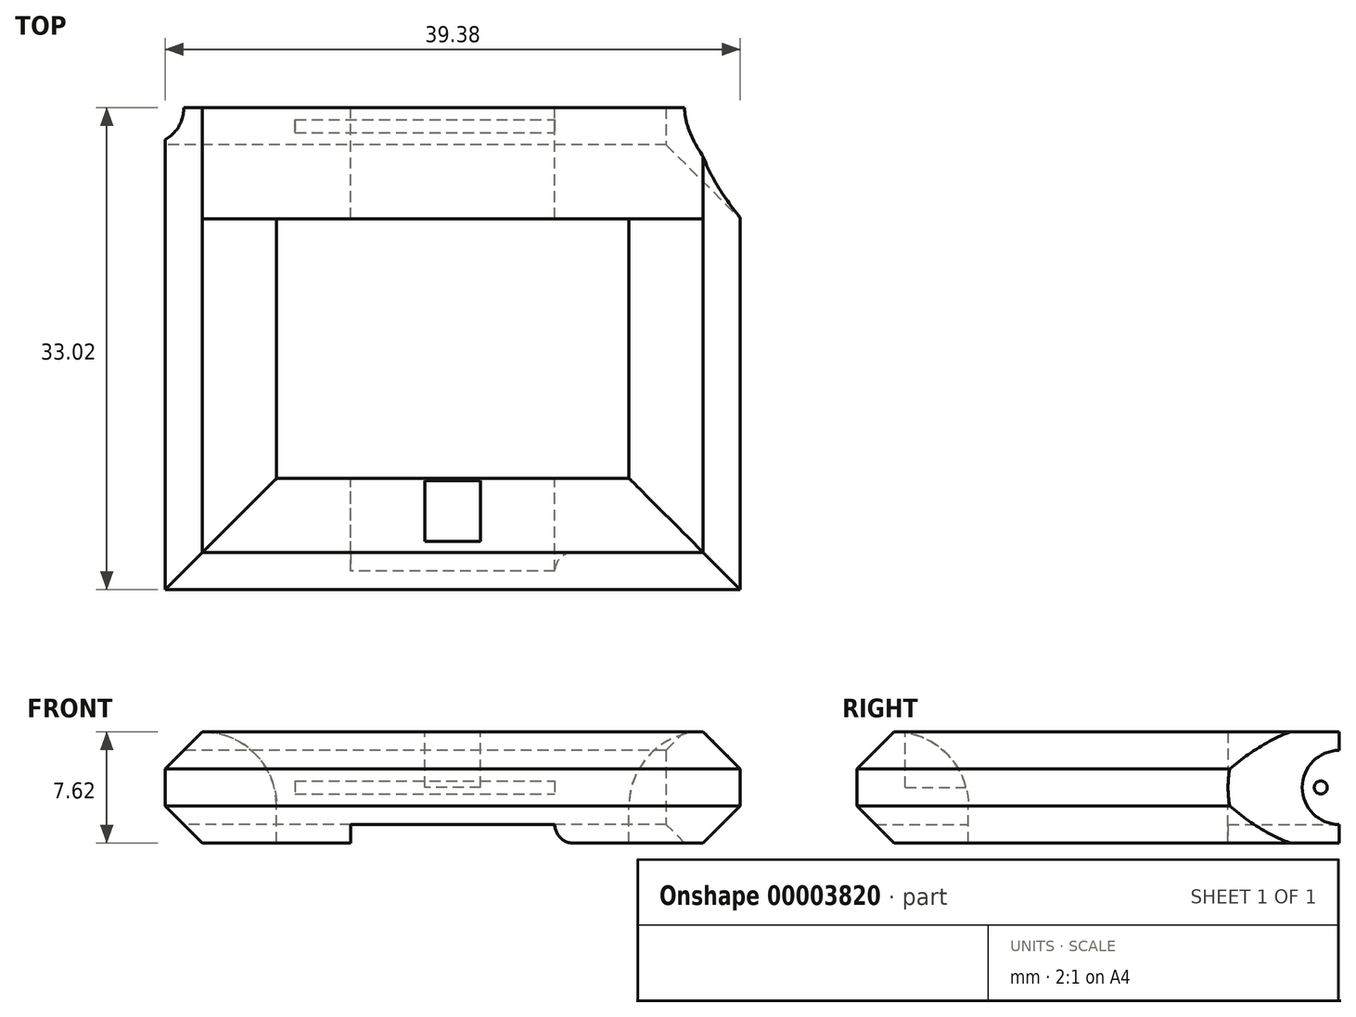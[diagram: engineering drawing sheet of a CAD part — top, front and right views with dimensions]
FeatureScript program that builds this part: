
annotation { "Feature Type Name" : "Feature", "Feature Type Description" : "" }
export const myFeature = defineFeature(function(context is Context, id is Id, definition is map)
    precondition{}
    {
        {
            var Q0;
            Q0=qCreatedBy(makeId("Right.planeOp"),FACE);
            var sketch = newSketch(context, id + "F0", { "sketchPlane" : qUnion([Q0])});
            skLineSegment(sketch, "E0.rect.bottom", {"start": v(3.8, -3.8) * mm, "end": v(-3.81, -3.81) * mm});
            skLineSegment(sketch, "E0.rect.top", {"start": v(3.8, 3.81) * mm, "end": v(-3.81, 3.81) * mm});
            skLineSegment(sketch, "E0.rect.left", {"start": v(3.8, -3.8) * mm, "end": v(3.81, 3.81) * mm});
            skLineSegment(sketch, "E0.rect.right", {"start": v(-3.81, -3.81) * mm, "end": v(-3.81, 3.8) * mm});
            skPoint(sketch, "E0.rect.middle", {"position": v(0, 0) * mm});
            skSolve(sketch);
        }
        {
            var Q0;
            Q0=qCreatedBy(makeId("Top.planeOp"),FACE);
            var sketch = newSketch(context, id + "F1", { "sketchPlane" : qUnion([Q0])});
            skLineSegment(sketch, "E1.bottom", {"start": v(15.87, 0) * mm, "end": v(-15.87, 0) * mm});
            skLineSegment(sketch, "E1.top", {"start": v(15.88, -25.4) * mm, "end": v(-15.87, -25.4) * mm});
            skLineSegment(sketch, "E1.left", {"start": v(15.88, 0) * mm, "end": v(15.88, -25.4) * mm});
            skLineSegment(sketch, "E1.right", {"start": v(-15.88, 0) * mm, "end": v(-15.87, -25.4) * mm});
            skSolve(sketch);
        }
        {
            var Q0;
            Q0=makeQuery(id+"F0.imprint","IMPRINT",FACE,{"disambiguationData":[TD([[makeQuery(id+"F0.imprint","IMPRINT",EDGE,{"derivedFrom":sQuery(id+"F0.wireOp",EDGE,"E0.rect.bottom")}),-1.0]])]});
            var Q1;
            Q1=sQuery(id+"F1.wireOp",EDGE,"E1.right");
            var Q2;
            Q2=sQuery(id+"F1.wireOp",EDGE,"E1.bottom");
            var Q3;
            Q3=sQuery(id+"F1.wireOp",EDGE,"E1.top");
            var Q4;
            Q4=sQuery(id+"F1.wireOp",EDGE,"E1.left");
            sweep(context, id + "F2", {"profiles" : qUnion([Q0]), "path" : qUnion([Q1, Q2, Q3, Q4])});
        }
        {
            var Q0;
            Q0=makeQuery(id+"F2.opSweep","SWEPT_FACE",FACE,{"disambiguationData":[OSD([sQuery(id+"F0.wireOp",EDGE,"E0.rect.left"),sQuery(id+"F1.wireOp",EDGE,"E1.right")])]});
            var sketch = newSketch(context, id + "F3", { "sketchPlane" : qUnion([Q0])});
            skArc(sketch, "E2", {"start": v(-3.81, -2.54) * mm, "mid": v(-1.27, 0) * mm, "end": v(-3.81, 2.54) * mm});
            skLineSegment(sketch, "E3", {"start": v(-3.81, 2.54) * mm, "end": v(-3.81, -2.54) * mm});
            skSolve(sketch);
        }
        {
            var Q0;
            Q0=makeQuery(id+"F3.imprint","IMPRINT",FACE,{"disambiguationData":[TD([[makeQuery(id+"F3.imprint","IMPRINT",EDGE,{"derivedFrom":sQuery(id+"F3.wireOp",EDGE,"E2")}),1.0]])]});
            var Q1;
            Q1=makeQuery(id+"F3.imprint","IMPRINT",FACE,{"disambiguationData":[TD([[makeQuery(id+"F3.imprint","IMPRINT",EDGE,{"derivedFrom":sQuery(id+"F3.wireOp",EDGE,"E2")}),1.0]])]});
            extrude(context, id + "F4", {"entities" : qUnion([Q0, Q1]), "operationType" : NewBodyOperationType.REMOVE, "endBound" : BoundingType.THROUGH_ALL, "oppositeDirection" : true, "depth" : 25.4 * mm});
        }
        {
            var Q0;
            Q0=makeQuery(id+"F2.opSweep","SWEPT_EDGE",EDGE,{"disambiguationData":[OSD([sQuery(id+"F0.wireOp",EDGE,"E0.rect.top"),sQuery(id+"F0.wireOp",EDGE,"E0.rect.left"),sQuery(id+"F1.wireOp",EDGE,"E1.left")])]});
            var Q1;
            Q1=makeQuery(id+"F2.opSweep","SWEPT_EDGE",EDGE,{"disambiguationData":[OSD([sQuery(id+"F0.wireOp",EDGE,"E0.rect.top"),sQuery(id+"F0.wireOp",EDGE,"E0.rect.left"),sQuery(id+"F1.wireOp",EDGE,"E1.top")])]});
            var Q2;
            Q2=makeQuery(id+"F2.opSweep","SWEPT_EDGE",EDGE,{"disambiguationData":[OSD([sQuery(id+"F0.wireOp",EDGE,"E0.rect.top"),sQuery(id+"F0.wireOp",EDGE,"E0.rect.left"),sQuery(id+"F1.wireOp",EDGE,"E1.right")])]});
            var Q3;
            Q3=makeQuery(id+"F2.opSweep","SWEPT_EDGE",EDGE,{"disambiguationData":[OSD([sQuery(id+"F0.wireOp",EDGE,"E0.rect.bottom"),sQuery(id+"F0.wireOp",EDGE,"E0.rect.left"),sQuery(id+"F1.wireOp",EDGE,"E1.right")])]});
            var Q4;
            Q4=makeQuery(id+"F2.opSweep","SWEPT_EDGE",EDGE,{"disambiguationData":[OSD([sQuery(id+"F0.wireOp",EDGE,"E0.rect.bottom"),sQuery(id+"F0.wireOp",EDGE,"E0.rect.left"),sQuery(id+"F1.wireOp",EDGE,"E1.top")])]});
            var Q5;
            Q5=makeQuery(id+"F2.opSweep","SWEPT_EDGE",EDGE,{"disambiguationData":[OSD([sQuery(id+"F0.wireOp",EDGE,"E0.rect.bottom"),sQuery(id+"F0.wireOp",EDGE,"E0.rect.left"),sQuery(id+"F1.wireOp",EDGE,"E1.left")])]});
            chamfer(context, id + "F5", {"entities" : qUnion([Q0, Q1, Q2, Q3, Q4, Q5]), "width" : 2.54 * mm, "tangentPropagation" : true});
        }
        {
            var Q0;
            Q0=makeQuery(id+"F2.opSweep","SWEPT_EDGE",EDGE,{"disambiguationData":[OSD([sQuery(id+"F0.wireOp",EDGE,"E0.rect.top"),sQuery(id+"F0.wireOp",EDGE,"E0.rect.right"),sQuery(id+"F1.wireOp",EDGE,"E1.top")])]});
            var Q1;
            Q1=makeQuery(id+"F2.opSweep","SWEPT_EDGE",EDGE,{"disambiguationData":[OSD([sQuery(id+"F0.wireOp",EDGE,"E0.rect.top"),sQuery(id+"F0.wireOp",EDGE,"E0.rect.right"),sQuery(id+"F1.wireOp",EDGE,"E1.right")])]});
            var Q2;
            Q2=makeQuery(id+"F2.opSweep","SWEPT_EDGE",EDGE,{"disambiguationData":[OSD([sQuery(id+"F0.wireOp",EDGE,"E0.rect.top"),sQuery(id+"F0.wireOp",EDGE,"E0.rect.right"),sQuery(id+"F1.wireOp",EDGE,"E1.left")])]});
            fillet(context, id + "F6", {"entities" : qUnion([Q0, Q1, Q2]), "radius" : 5.08 * mm, "tangentPropagation" : true, "allowEdgeOverflow" : false});
        }
        {
            var Q0;
            Q0=makeQuery(id+"F2.opSweep","SWEPT_FACE",FACE,{"disambiguationData":[OSD([sQuery(id+"F0.wireOp",EDGE,"E0.rect.top"),sQuery(id+"F1.wireOp",EDGE,"E1.bottom")])]});
            var sketch = newSketch(context, id + "F7", { "sketchPlane" : qUnion([Q0])});
            skLineSegment(sketch, "E4.bottom", {"start": v(-6.98, -3.81) * mm, "end": v(6.98, -3.81) * mm});
            skLineSegment(sketch, "E4.top", {"start": v(-6.98, -1.27) * mm, "end": v(6.98, -1.27) * mm});
            skLineSegment(sketch, "E4.left", {"start": v(-6.98, -3.81) * mm, "end": v(-6.98, -1.27) * mm});
            skLineSegment(sketch, "E4.right", {"start": v(6.98, -3.81) * mm, "end": v(6.98, -1.27) * mm});
            skSolve(sketch);
        }
        {
            var Q0;
            Q0=makeQuery(id+"F7.imprint","IMPRINT",FACE,{"disambiguationData":[TD([[makeQuery(id+"F7.imprint","IMPRINT",EDGE,{"derivedFrom":sQuery(id+"F7.wireOp",EDGE,"E4.bottom")}),-1.0]])]});
            extrude(context, id + "F8", {"entities" : qUnion([Q0]), "operationType" : NewBodyOperationType.REMOVE, "endBound" : BoundingType.THROUGH_ALL, "oppositeDirection" : true, "depth" : 25.4 * mm});
        }
        {
            var Q0;
            Q0=makeQuery(id+"F8.boolean.opBoolean","COPY",FACE,{"derivedFrom":makeQuery(id+"F8.opExtrude","SWEPT_FACE",FACE,{"disambiguationData":[OSD([sQuery(id+"F7.wireOp",EDGE,"E4.left")])]})});
            var sketch = newSketch(context, id + "F9", { "sketchPlane" : qUnion([Q0])});
            skCircle(sketch, "E5", {"center": v(-2.54, 0) * mm, "radius": 0.44 * mm});
            skSolve(sketch);
        }
        {
            var Q0;
            Q0=makeQuery(id+"F9.imprint","IMPRINT",FACE,{"disambiguationData":[TD([[makeQuery(id+"F9.imprint","IMPRINT",EDGE,{"derivedFrom":sQuery(id+"F9.wireOp",EDGE,"E5")}),1.0]])]});
            extrude(context, id + "F10", {"entities" : qUnion([Q0]), "operationType" : NewBodyOperationType.ADD, "depth" : 17.78 * mm});
        }
        {
            var Q0;
            Q0=makeQuery(id+"F8.boolean.opBoolean","COPY",EDGE,{"derivedFrom":makeQuery(id+"F8.opExtrude","CAP_EDGE",EDGE,{"disambiguationData":[OSD([sQuery(id+"F7.wireOp",EDGE,"E4.top")])],"isStart":true})});
            var Q1;
            Q1=makeQuery(id+"F8.boolean.opBoolean","COPY",EDGE,{"derivedFrom":makeQuery(id+"F8.opExtrude","SWEPT_EDGE",EDGE,{"disambiguationData":[OSD([sQuery(id+"F0.wireOp",EDGE,"E0.rect.top"),sQuery(id+"F0.wireOp",EDGE,"E0.rect.right"),sQuery(id+"F1.wireOp",EDGE,"E1.bottom"),sQuery(id+"F7.wireOp",EDGE,"E4.bottom"),sQuery(id+"F7.wireOp",EDGE,"E4.left")])]})});
            var Q2;
            Q2=makeQuery(id+"F8.boolean.opBoolean","COPY",EDGE,{"derivedFrom":makeQuery(id+"F8.opExtrude","SWEPT_EDGE",EDGE,{"disambiguationData":[OSD([sQuery(id+"F0.wireOp",EDGE,"E0.rect.top"),sQuery(id+"F0.wireOp",EDGE,"E0.rect.right"),sQuery(id+"F1.wireOp",EDGE,"E1.bottom"),sQuery(id+"F7.wireOp",EDGE,"E4.bottom"),sQuery(id+"F7.wireOp",EDGE,"E4.right")])]})});
            var Q3;
            Q3=makeQuery(id+"F8.boolean.opBoolean","INTERSECT",EDGE,{"derivedFrom":[makeQuery(id+"F2.opSweep","SWEPT_FACE",FACE,{"disambiguationData":[OSD([sQuery(id+"F0.wireOp",EDGE,"E0.rect.bottom"),sQuery(id+"F1.wireOp",EDGE,"E1.bottom")])]}),makeQuery(id+"F8.opExtrude","SWEPT_FACE",FACE,{"disambiguationData":[OSD([sQuery(id+"F7.wireOp",EDGE,"E4.top")])]})]});
            fillet(context, id + "F11", {"entities" : qUnion([Q0, Q1, Q2, Q3]), "radius" : 1.27 * mm, "tangentPropagation" : true, "allowEdgeOverflow" : false});
        }
        {
            var Q0;
            Q0=qCreatedBy(makeId("Top.planeOp"),FACE);
            cPlane(context, id + "F12", {"entities" : qUnion([Q0]), "cplaneType" : CPlaneType.OFFSET, "offset" : 25.4 * mm, "width" : 152.4 * mm, "height" : 152.4 * mm});
        }
        {
            var Q0;
            Q0=qCreatedBy(id+"F12.planeOp",FACE);
            var sketch = newSketch(context, id + "F13", { "sketchPlane" : qUnion([Q0])});
            skLineSegment(sketch, "E6", {"start": v(0, 0) * mm, "end": v(0, -31.12) * mm, "construction": true});
            skLineSegment(sketch, "E7.rect.bottom", {"start": v(1.9, -25.9) * mm, "end": v(-1.9, -25.9) * mm});
            skLineSegment(sketch, "E7.rect.top", {"start": v(1.9, -21.08) * mm, "end": v(-1.9, -21.08) * mm});
            skLineSegment(sketch, "E7.rect.left", {"start": v(1.9, -25.9) * mm, "end": v(1.9, -21.08) * mm});
            skLineSegment(sketch, "E7.rect.right", {"start": v(-1.9, -25.9) * mm, "end": v(-1.9, -21.08) * mm});
            skPoint(sketch, "E7.rect.middle", {"position": v(0, -23.5) * mm});
            skSolve(sketch);
        }
        {
            var Q0;
            Q0=makeQuery(id+"F13.imprint","IMPRINT",FACE,{"disambiguationData":[TD([[makeQuery(id+"F13.imprint","IMPRINT",EDGE,{"derivedFrom":sQuery(id+"F13.wireOp",EDGE,"E7.rect.bottom")}),-1.0]])]});
            extrude(context, id + "F14", {"entities" : qUnion([Q0]), "operationType" : NewBodyOperationType.REMOVE, "oppositeDirection" : true, "depth" : 25.4 * mm});
        }
        {
            var Q0;
            Q0=makeQuery(id+"F4.boolean.opBoolean","INTERSECT",EDGE,{"derivedFrom":[makeQuery(id+"F2.opSweep","SWEPT_FACE",FACE,{"disambiguationData":[OSD([sQuery(id+"F0.wireOp",EDGE,"E0.rect.left"),sQuery(id+"F1.wireOp",EDGE,"E1.left")])]}),makeQuery(id+"F4.opExtrude","SWEPT_FACE",FACE,{"disambiguationData":[OSD([sQuery(id+"F3.wireOp",EDGE,"E2")])]})]});
            var Q1;
            Q1=makeQuery(id+"F4.boolean.opBoolean","COPY",EDGE,{"derivedFrom":makeQuery(id+"F4.opExtrude","CAP_EDGE",EDGE,{"disambiguationData":[OSD([sQuery(id+"F3.wireOp",EDGE,"E2")])],"isStart":true})});
            chamfer(context, id + "F15", {"entities" : qUnion([Q0, Q1]), "width" : 5.08 * mm, "tangentPropagation" : true});
        }
    });
